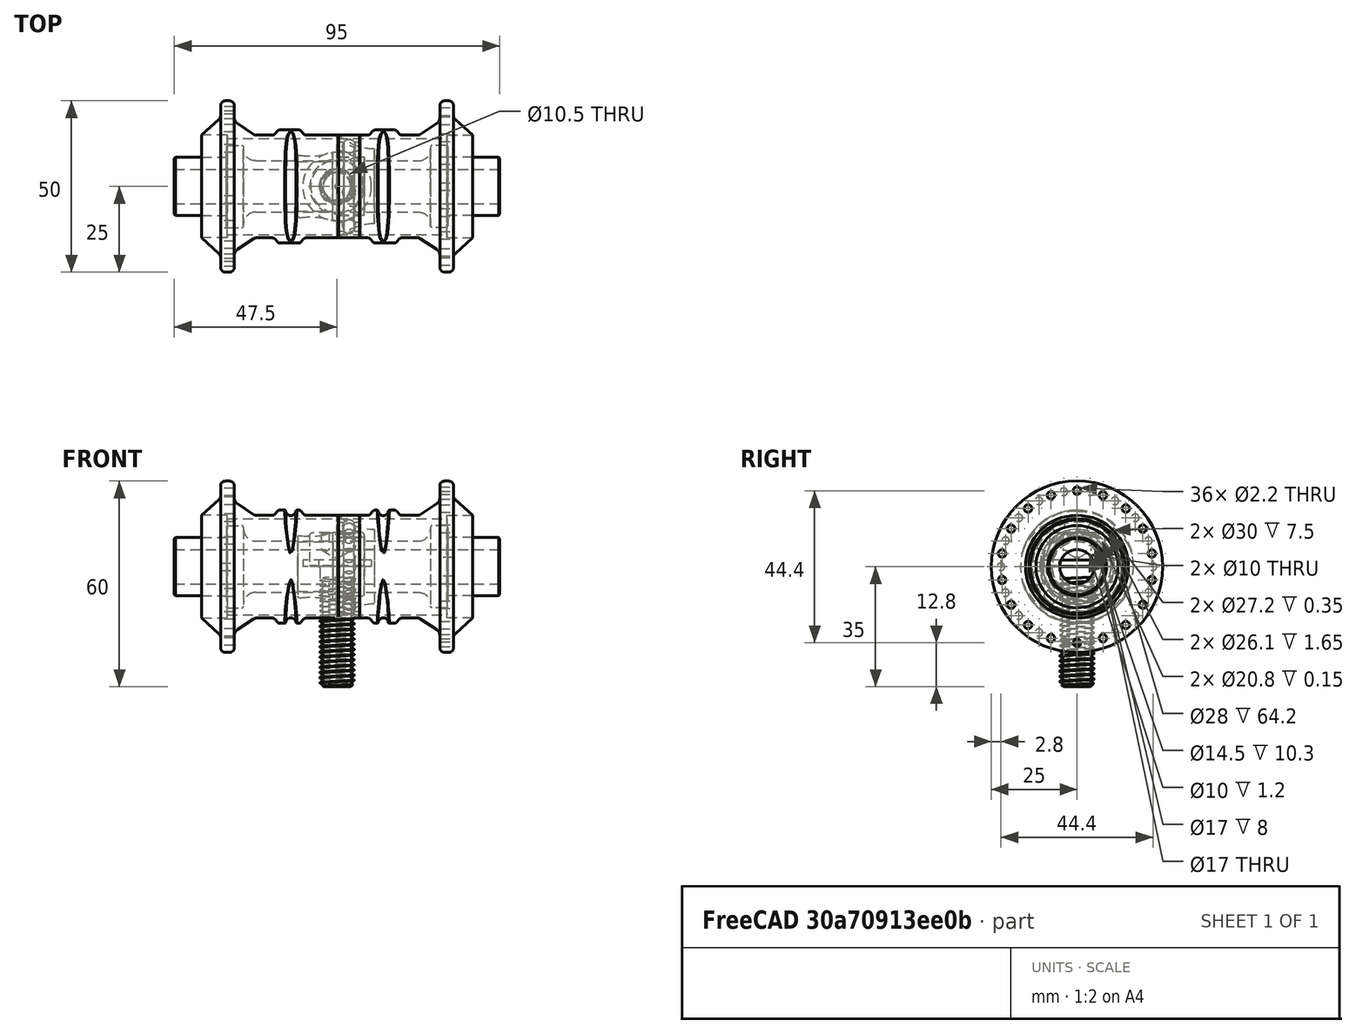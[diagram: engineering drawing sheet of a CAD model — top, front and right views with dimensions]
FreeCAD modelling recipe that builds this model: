
FCSTD DOCUMENT  (FreeCAD 1.0R39109 (Git))
Label: Bike Hub
License: All rights reserved
LicenseURL: https://en.wikipedia.org/wiki/All_rights_reserved
objects: App::FeaturePython×16, Part::Feature×15, Sketcher::SketchObject×13, App::Link×12, PartDesign::Pocket×6, PartDesign::Revolution×4, PartDesign::Body×4, PartDesign::Hole×2, PartDesign::Mirrored×2, PartDesign::PolarPattern×2, PartDesign::Fillet×2, Part::FeaturePython×2, PartDesign::Plane×1, PartDesign::SubtractivePipe×1, App::Part×1, App::DocumentObjectGroup×1, Assembly::JointGroup×1, Assembly::ViewGroup×1, Assembly::AssemblyObject×1
note: 101 computed .brp shape members not serialized (recipe doc carries the construction recipe); baked Part::Feature solids carry a one-line shape summary decoded from their .brp

FEATURE [Sketcher::SketchObject] Sketch
  ArcFitTolerance = 1e-06
  AttachmentSupport = -> [XZ_Plane]
  FullyConstrained = true
  MakeInternals = false
  MapMode = 5
  Placement = pos=(0,0,0) rot=(1,0,0;1.5708rad)
  sketch-geometry (19):
    g0: LineSegment StartX=0 StartY=0 StartZ=0 EndX=-47.5 EndY=0 EndZ=0
    g1: LineSegment StartX=-47.5 StartY=0 StartZ=0 EndX=-47.5 EndY=8.14645 EndZ=0
    g2: LineSegment StartX=-47.1464 StartY=8.5 StartZ=0 EndX=-32.8 EndY=8.5 EndZ=0
    g3: LineSegment StartX=-32.3 StartY=9 StartZ=0 EndX=-32.3 EndY=11.5 EndZ=0
    g4: LineSegment StartX=-31.8 StartY=12 StartZ=0 EndX=-27.8 EndY=12 EndZ=0
    g5: LineSegment StartX=-27.3 StartY=11.5 StartZ=0 EndX=-27.3 EndY=11 EndZ=0
    g6: LineSegment StartX=-23.8 StartY=7.5 StartZ=0 EndX=0 EndY=7.5 EndZ=0
    g7: LineSegment StartX=0 StartY=7.5 StartZ=0 EndX=0 EndY=0 EndZ=0
    g8: ArcOfCircle CenterX=-27.8 CenterY=11.5 CenterZ=0 NormalX=0 NormalY=0 NormalZ=1 AngleXU=0 Radius=0.5 StartAngle=0 EndAngle=1.5708
    g9: GeomPoint [constr] X=-27.3 Y=12 Z=0
    g10: ArcOfCircle CenterX=-23.8 CenterY=11 CenterZ=0 NormalX=0 NormalY=0 NormalZ=1 AngleXU=0 Radius=3.5 StartAngle=3.14159 EndAngle=4.71239
    g11: GeomPoint [constr] X=-27.3 Y=7.5 Z=0
    g12: ArcOfCircle CenterX=-31.8 CenterY=11.5 CenterZ=0 NormalX=0 NormalY=0 NormalZ=1 AngleXU=0 Radius=0.5 StartAngle=1.5708 EndAngle=3.14159
    g13: GeomPoint [constr] X=-32.3 Y=12 Z=0
    g14: ArcOfCircle CenterX=-32.8 CenterY=9 CenterZ=0 NormalX=0 NormalY=0 NormalZ=1 AngleXU=0 Radius=0.5 StartAngle=4.71239 EndAngle=6.28319
    g15: GeomPoint [constr] X=-32.3 Y=8.5 Z=0
    g16: ArcOfCircle [constr] CenterX=-47.1464 CenterY=8.14645 CenterZ=0 NormalX=0 NormalY=0 NormalZ=1 AngleXU=0 Radius=0.353553 StartAngle=1.5708 EndAngle=3.14159
    g17: GeomPoint [constr] X=-47.5 Y=8.5 Z=0
    g18: LineSegment StartX=-47.1464 StartY=8.5 StartZ=0 EndX=-47.5 EndY=8.14645 EndZ=0
  constraints (45):
    c: Coincident(g-1,g0)
    c: PointOnObject(g0,g-1)
    c: Coincident(g0,g1)
    c: Vertical(g1)
    c: Horizontal(g2)
    c: Horizontal(g4)
    c: Vertical(g5)
    c: Horizontal(g6)
    c: Coincident(g6,g7)
    c: Coincident(g7,g0)
    c: Vertical(g7)
    c: Vertical(g3)
    c: DistanceX(g0,g0) = 47.5
    c: DistanceY(g1,g17) = 8.5
    c: Distance(g13,g0) = 12
    c: DistanceX(g13,g-1) = 32.3
    c: DistanceX(g13,g9) = 5
    c: DistanceY(g7,g7) = 7.5
    c: PointOnObject(g9,g4)
    c: PointOnObject(g9,g5)
    c: Tangent(g4,g8) = 1.5708
    c: Tangent(g5,g8) = 1.5708
    c: PointOnObject(g11,g5)
    c: PointOnObject(g11,g6)
    c: Tangent(g5,g10) = -1.5708
    c: Tangent(g6,g10) = -1.5708
    c: PointOnObject(g13,g3)
    c: PointOnObject(g13,g4)
    c: Tangent(g3,g12) = 1.5708
    c: Tangent(g4,g12) = 1.5708
    c: PointOnObject(g15,g2)
    c: PointOnObject(g15,g3)
    c: Tangent(g2,g14) = -1.5708
    c: Tangent(g3,g14) = -1.5708
    c: Radius(g8) = 0.5
    c: Equal(g8,g12)
    c: Equal(g12,g14)
    c: Radius(g10) = 3.5
    c: PointOnObject(g17,g1)
    c: PointOnObject(g17,g2)
    c: Tangent(g1,g16) = 1.5708
    c: Tangent(g2,g16) = 1.5708
    c: Coincident(g18,g1)
    c: Coincident(g18,g2)
    c: Distance(g18,g18) = 0.5
FEATURE [PartDesign::Revolution] Revolution
  Angle = 360
  Angle2 = 60
  Axis = (1,0,0)
  Base = (0,0,0)
  Placement = pos=(0,0,0) rot=(1,0,0;1.5708rad)
  Profile = -> Sketch
  ReferenceAxis = -> X_Axis
  Refine = true
  Suppressed = false
  Type = 0
FEATURE [PartDesign::Hole] Hole
  BaseFeature = -> Revolution
  CustomThreadClearance = 0
  Depth = 117.922
  DepthType = 1
  Diameter = 10
  DrillForDepth = false
  DrillPoint = 1
  DrillPointAngle = 118
  HoleCutCountersinkAngle = 90
  HoleCutCustomValues = false
  HoleCutDepth = 0
  HoleCutDiameter = 6.1
  HoleCutType = 0
  ModelThread = false
  Placement = pos=(0,0,0) rot=(1,0,0;1.5708rad)
  Profile = -> Revolution [Face5]
  Refine = true
  Suppressed = false
  Tapered = false
  TaperedAngle = 90
  ThreadClass = 0
  ThreadDepth = 117.922
  ThreadDepthType = 0
  ThreadDirection = 0
  ThreadFit = 0
  ThreadSize = 0
  ThreadType = 0
  Threaded = false
  UseCustomThreadClearance = false
FEATURE [PartDesign::Mirrored] Mirrored
  BaseFeature = -> Hole
  MirrorPlane = -> YZ_Plane
  Originals = -> [Hole]
  Placement = pos=(0,0,0) rot=(1,0,0;1.5708rad)
  Refine = true
  Suppressed = false
  TransformMode = 1
FEATURE [PartDesign::Body] Body  label="Axle"
  AllowCompound = false
  Group = -> [Sketch,Revolution,Hole,Mirrored]
  Origin = -> Origin
  Tip = -> Mirrored
FEATURE [Sketcher::SketchObject] Sketch001
  ArcFitTolerance = 1e-06
  AttachmentSupport = -> [XZ_Plane001]
  FullyConstrained = true
  MakeInternals = false
  MapMode = 5
  Placement = pos=(0,0,0) rot=(1,0,0;1.5708rad)
  sketch-geometry (31):
    g0: LineSegment StartX=0 StartY=0 StartZ=0 EndX=-39.6 EndY=0 EndZ=0
    g1: LineSegment StartX=-39.6 StartY=0 StartZ=0 EndX=-39.6 EndY=15 EndZ=0
    g2: LineSegment StartX=-39.6 StartY=15 StartZ=0 EndX=-34.4676 EndY=19.5825 EndZ=0
    g3: LineSegment StartX=-34 StartY=20.6268 StartZ=0 EndX=-34 EndY=23.6 EndZ=0
    g4: LineSegment StartX=-32.6 StartY=25 StartZ=0 EndX=-31.4 EndY=25 EndZ=0
    g5: LineSegment StartX=-30 StartY=23.6 StartZ=0 EndX=-30 EndY=20.0704 EndZ=0
    g6: LineSegment StartX=-29.1094 StartY=18.4063 StartZ=0 EndX=-24.2519 EndY=15.1679 EndZ=0
    g7: LineSegment StartX=-23.6972 StartY=15 StartZ=0 EndX=-18.8806 EndY=15 EndZ=0
    g8: LineSegment StartX=-18.0998 StartY=15.3753 StartZ=0 EndX=-17.5002 EndY=16.1247 EndZ=0
    g9: LineSegment StartX=-16.7194 StartY=16.5 StartZ=0 EndX=-11.1806 EndY=16.5 EndZ=0
    g10: LineSegment StartX=-10.3998 StartY=16.1247 StartZ=0 EndX=-9.80024 EndY=15.3753 EndZ=0
    g11: LineSegment StartX=-9.01938 StartY=15 StartZ=0 EndX=0 EndY=15 EndZ=0
    g12: LineSegment StartX=0 StartY=15 StartZ=0 EndX=0 EndY=0 EndZ=0
    g13: ArcOfCircle CenterX=-32.6 CenterY=23.6 CenterZ=0 NormalX=0 NormalY=0 NormalZ=1 AngleXU=0 Radius=1.4 StartAngle=1.5708 EndAngle=3.14159
    g14: GeomPoint [constr] X=-34 Y=25 Z=0
    g15: ArcOfCircle CenterX=-31.4 CenterY=23.6 CenterZ=0 NormalX=0 NormalY=0 NormalZ=1 AngleXU=0 Radius=1.4 StartAngle=0 EndAngle=1.5708
    g16: GeomPoint [constr] X=-30 Y=25 Z=0
    g17: ArcOfCircle CenterX=-35.4 CenterY=20.6268 CenterZ=0 NormalX=0 NormalY=0 NormalZ=1 AngleXU=0 Radius=1.4 StartAngle=5.44124 EndAngle=6.28319
    g18: GeomPoint [constr] X=-34 Y=20 Z=0
    g19: ArcOfCircle CenterX=-28 CenterY=20.0704 CenterZ=0 NormalX=0 NormalY=0 NormalZ=1 AngleXU=0 Radius=2 StartAngle=3.14159 EndAngle=4.12439
    g20: GeomPoint [constr] X=-30 Y=19 Z=0
    g21: ArcOfCircle CenterX=-23.6972 CenterY=16 CenterZ=0 NormalX=0 NormalY=0 NormalZ=1 AngleXU=0 Radius=1 StartAngle=4.12439 EndAngle=4.71239
    g22: GeomPoint [constr] X=-24 Y=15 Z=0
    g23: ArcOfCircle CenterX=-18.8806 CenterY=16 CenterZ=0 NormalX=0 NormalY=0 NormalZ=1 AngleXU=0 Radius=1 StartAngle=4.71239 EndAngle=5.60844
    g24: GeomPoint [constr] X=-18.4 Y=15 Z=0
    g25: ArcOfCircle CenterX=-16.7194 CenterY=15.5 CenterZ=0 NormalX=0 NormalY=0 NormalZ=1 AngleXU=0 Radius=1 StartAngle=1.5708 EndAngle=2.46685
    g26: GeomPoint [constr] X=-17.2 Y=16.5 Z=0
    g27: ArcOfCircle CenterX=-11.1806 CenterY=15.5 CenterZ=0 NormalX=0 NormalY=0 NormalZ=1 AngleXU=0 Radius=1 StartAngle=0.674741 EndAngle=1.5708
    g28: GeomPoint [constr] X=-10.7 Y=16.5 Z=0
    g29: ArcOfCircle CenterX=-9.01938 CenterY=16 CenterZ=0 NormalX=0 NormalY=0 NormalZ=1 AngleXU=0 Radius=1 StartAngle=3.81633 EndAngle=4.71239
    g30: GeomPoint [constr] X=-9.5 Y=15 Z=0
  constraints (74):
    c: Coincident(g-1,g0)
    c: PointOnObject(g0,g-1)
    c: Coincident(g0,g1)
    c: Vertical(g1)
    c: Coincident(g1,g2)
    c: Vertical(g3)
    c: Horizontal(g4)
    c: Vertical(g5)
    c: Horizontal(g7)
    c: Horizontal(g9)
    c: Horizontal(g11)
    c: Coincident(g11,g12)
    c: Coincident(g12,g0)
    c: Vertical(g12)
    c: DistanceX(g0,g0) = 39.6
    c: Distance(g0,g4) = 25
    c: DistanceY(g-1,g1) = 15
    c: DistanceY(g-1,g18) = 20
    c: DistanceY(g-1,g20) = 19
    c: DistanceX(g14,g16) = 4
    c: DistanceX(g14,g-1) = 34
    c: DistanceX(g22,g-1) = 24
    c: DistanceX(g26,g28) = 6.5
    c: DistanceX(g30,g11) = 9.5
    c: DistanceX(g28,g-1) = 10.7
    c: DistanceY(g-1,g28) = 16.5
    c: PointOnObject(g14,g3)
    c: PointOnObject(g14,g4)
    c: Tangent(g3,g13) = 1.5708
    c: Tangent(g4,g13) = 1.5708
    c: PointOnObject(g16,g4)
    c: PointOnObject(g16,g5)
    c: Tangent(g4,g15) = 1.5708
    c: Tangent(g5,g15) = 1.5708
    c: PointOnObject(g18,g2)
    c: PointOnObject(g18,g3)
    c: Tangent(g2,g17) = -1.5708
    c: Tangent(g3,g17) = -1.5708
    c: PointOnObject(g20,g5)
    c: PointOnObject(g20,g6)
    c: Tangent(g5,g19) = -1.5708
    c: Tangent(g6,g19) = -1.5708
    c: Equal(g17,g13)
    c: Equal(g13,g15)
    c: Radius(g13) = 1.4
    c: Radius(g19) = 2
    c: PointOnObject(g22,g6)
    c: PointOnObject(g22,g7)
    c: Tangent(g6,g21) = -1.5708
    c: Tangent(g7,g21) = -1.5708
    c: PointOnObject(g24,g7)
    c: PointOnObject(g24,g8)
    c: Tangent(g7,g23) = -1.5708
    c: Tangent(g8,g23) = -1.5708
    c: PointOnObject(g26,g8)
    c: PointOnObject(g26,g9)
    c: Tangent(g8,g25) = 1.5708
    c: Tangent(g9,g25) = 1.5708
    c: PointOnObject(g28,g9)
    c: PointOnObject(g28,g10)
    c: Tangent(g9,g27) = 1.5708
    c: Tangent(g10,g27) = 1.5708
    c: PointOnObject(g30,g10)
    c: PointOnObject(g30,g11)
    c: Tangent(g10,g29) = -1.5708
    c: Tangent(g11,g29) = -1.5708
    c: Radius(g21) = 1
    c: Horizontal(g11,g22)
    c: Equal(g21,g23)
    c: Equal(g23,g25)
    c: Equal(g25,g27)
    c: Equal(g27,g29)
    c: Horizontal(g11,g1)
    c: Equal(g8,g10)
FEATURE [PartDesign::Revolution] Revolution001
  Angle = 360
  Angle2 = 60
  Axis = (1,0,0)
  Base = (0,0,0)
  Placement = pos=(0,0,0) rot=(1,0,0;1.5708rad)
  Profile = -> Sketch001
  ReferenceAxis = -> X_Axis001
  Refine = true
  Suppressed = false
  Type = 0
FEATURE [Sketcher::SketchObject] Sketch002
  ArcFitTolerance = 1e-06
  AttachmentSupport = -> [Revolution001]
  FullyConstrained = true
  MakeInternals = false
  MapMode = 5
  Placement = pos=(-39.6,0,0) rot=(0.707107,0,-0.707107;3.14159rad)
  sketch-geometry (1):
    g0: Circle CenterX=0 CenterY=0 CenterZ=0 NormalX=0 NormalY=0 NormalZ=1 AngleXU=0 Radius=15
  constraints (2):
    c: Diameter(g0) = 30
    c: Coincident(g0,g-1)
FEATURE [PartDesign::Pocket] Pocket
  BaseFeature = -> Revolution001
  Direction = (1,0,2e-16)
  Length = 7.5
  Length2 = 5
  Placement = pos=(0,0,0) rot=(1,0,0;1.5708rad)
  Profile = -> Sketch002
  ReferenceAxis = -> Sketch002 [N_Axis]
  Refine = true
  Suppressed = false
  Type = 0
FEATURE [Sketcher::SketchObject] Sketch003
  ArcFitTolerance = 1e-06
  AttachmentSupport = -> [Pocket]
  FullyConstrained = true
  MakeInternals = false
  MapMode = 5
  Placement = pos=(0,0,0) rot=(0.707107,0,0.707107;3.14159rad)
  sketch-geometry (1):
    g0: Circle CenterX=0 CenterY=0 CenterZ=0 NormalX=0 NormalY=0 NormalZ=1 AngleXU=0 Radius=14
  constraints (2):
    c: Diameter(g0) = 28
    c: Coincident(g0,g-1)
FEATURE [PartDesign::Pocket] Pocket001
  BaseFeature = -> Pocket
  Direction = (-1,0,2e-16)
  Length = 5
  Length2 = 5
  Placement = pos=(0,0,0) rot=(1,0,0;1.5708rad)
  Profile = -> Sketch003
  ReferenceAxis = -> Sketch003 [N_Axis]
  Refine = true
  Suppressed = false
  Type = 1
FEATURE [PartDesign::Plane] DatumPlane
  AttachmentOffset = pos=(0,0,-13.5) rot=(0,0,1;0rad)
  AttachmentSupport = -> [Pocket001]
  Length = 60
  MapMode = 5
  Placement = pos=(-13.5,0,3e-15) rot=(0.707107,0,0.707107;3.14159rad)
  ResizeMode = 0
  Width = 60
FEATURE [Sketcher::SketchObject] Sketch004
  ArcFitTolerance = 1e-06
  AttachmentSupport = -> [DatumPlane]
  FullyConstrained = true
  MakeInternals = false
  MapMode = 5
  Placement = pos=(-13.5,0,3e-15) rot=(0.707107,0,0.707107;3.14159rad)
  sketch-geometry (5):
    g0: Ellipse CenterX=0 CenterY=0 CenterZ=0 NormalX=0 NormalY=0 NormalZ=1 MajorRadius=18.1 MinorRadius=16.4 AngleXU=-1.5708
    g1: LineSegment [constr] StartX=6.27002e-06 StartY=-18.1 StartZ=0 EndX=-6.27002e-06 EndY=18.1 EndZ=0
    g2: LineSegment [constr] StartX=16.4 StartY=5.68113e-06 StartZ=0 EndX=-16.4 EndY=-5.68113e-06 EndZ=0
    g3: GeomPoint [constr] X=2.65292e-06 Y=-7.65833 Z=0
    g4: GeomPoint [constr] X=-2.65292e-06 Y=7.65833 Z=0
  constraints (5):
    c: InternalAlignment(g1-g4 -> g0) x4
    c: Distance(g0,g2) = 16.4
    c: Angle(g2) = 3.14159
    c: Distance(g0,g1) = 18.1
    c: Coincident(g0,g-1)
FEATURE [Sketcher::SketchObject] Sketch005
  ArcFitTolerance = 1e-06
  AttachmentSupport = -> [XY_Plane001]
  ExternalGeometry = -> [Sketch004]
  FullyConstrained = true
  MakeInternals = false
  MapMode = 5
  sketch-geometry (1):
    g0: Circle CenterX=-13.5 CenterY=18.1 CenterZ=0 NormalX=0 NormalY=0 NormalZ=1 AngleXU=0 Radius=1.5
  constraints (2):
    c: Diameter(g0) = 3
    c: Coincident(g0,g-3)
FEATURE [PartDesign::SubtractivePipe] SubtractivePipe
  AuxilleryCurvelinear = true
  AuxillerySpineTangent = false
  BaseFeature = -> Pocket001
  Binormal = (0,0,0)
  Mode = 0
  Placement = pos=(0,0,0) rot=(1,0,0;1.5708rad)
  Profile = -> Sketch005
  Refine = true
  Spine = -> Sketch004
  SpineTangent = false
  Suppressed = false
  Transformation = 0
  Transition = 0
FEATURE [PartDesign::Mirrored] Mirrored001
  BaseFeature = -> SubtractivePipe
  MirrorPlane = -> Sketch005 [V_Axis]
  Originals = -> [SubtractivePipe]
  Placement = pos=(0,0,0) rot=(1,0,0;1.5708rad)
  Refine = true
  Suppressed = false
  TransformMode = 1
FEATURE [Sketcher::SketchObject] Sketch006
  ArcFitTolerance = 1e-06
  AttachmentSupport = -> [Mirrored001]
  FullyConstrained = true
  MakeInternals = false
  MapMode = 5
  Placement = pos=(-34,0,0) rot=(0.707107,0,-0.707107;3.14159rad)
  sketch-geometry (1):
    g0: Circle CenterX=0 CenterY=22.2 CenterZ=0 NormalX=0 NormalY=0 NormalZ=1 AngleXU=0 Radius=1.1
  constraints (3):
    c: Diameter(g0) = 2.2
    c: PointOnObject(g0,g-2)
    c: DistanceY(g-1,g0) = 22.2
FEATURE [PartDesign::Pocket] Pocket002
  BaseFeature = -> Mirrored001
  Direction = (1,0,2e-16)
  Length = 0
  Length2 = 5
  Placement = pos=(0,0,0) rot=(1,0,0;1.5708rad)
  Profile = -> Sketch006
  ReferenceAxis = -> Sketch006 [N_Axis]
  Refine = true
  Suppressed = false
  Type = 3
  UpToFace = -> Mirrored001 [Face14]
FEATURE [PartDesign::PolarPattern] PolarPattern
  Angle = 360
  Axis = -> Sketch006 [N_Axis]
  BaseFeature = -> Pocket002
  Mode = 0
  Occurrences = 18
  Offset = 120
  Originals = -> [Pocket002]
  Placement = pos=(0,0,0) rot=(1,0,0;1.5708rad)
  Refine = true
  Suppressed = false
  TransformMode = 0
FEATURE [Sketcher::SketchObject] Sketch007
  ArcFitTolerance = 1e-06
  AttachmentSupport = -> [PolarPattern]
  FullyConstrained = true
  MakeInternals = false
  MapMode = 5
  Placement = pos=(34,0,0) rot=(0.707107,0,0.707107;3.14159rad)
  sketch-geometry (2):
    g0: Circle CenterX=-3.85499 CenterY=21.8627 CenterZ=0 NormalX=0 NormalY=0 NormalZ=1 AngleXU=0 Radius=1.1
    g1: LineSegment [constr] StartX=-3.85499 StartY=21.8627 StartZ=0 EndX=4e-16 EndY=0 EndZ=0
  constraints (5):
    c: Diameter(g0) = 2.2
    c: Coincident(g1,g0)
    c: Coincident(g1,g-1)
    c: Distance(g1,g1) = 22.2
    c: Angle(g-2,g1) = 0.174533
FEATURE [PartDesign::Pocket] Pocket003
  BaseFeature = -> PolarPattern
  Direction = (-1,0,2e-16)
  Length = 0
  Length2 = 5
  Placement = pos=(0,0,0) rot=(1,0,0;1.5708rad)
  Profile = -> Sketch007
  ReferenceAxis = -> Sketch007 [N_Axis]
  Refine = true
  Suppressed = false
  Type = 3
  UpToFace = -> PolarPattern [Face53]
FEATURE [PartDesign::PolarPattern] PolarPattern001
  Angle = 360
  Axis = -> Sketch007 [N_Axis]
  BaseFeature = -> Pocket003
  Mode = 0
  Occurrences = 18
  Offset = 120
  Originals = -> [Pocket003]
  Placement = pos=(0,0,0) rot=(1,0,0;1.5708rad)
  Refine = true
  Suppressed = false
  TransformMode = 0
FEATURE [PartDesign::Fillet] Fillet
  Base = -> PolarPattern001 [Edge9,Edge15,Edge41,Edge35]
  BaseFeature = -> PolarPattern001
  Placement = pos=(0,0,0) rot=(1,0,0;1.5708rad)
  Radius = 0.3
  Refine = true
  SupportTransform = false
  Suppressed = false
  UseAllEdges = false
FEATURE [PartDesign::Body] Body001  label="Hub Cage"
  AllowCompound = false
  Group = -> [Sketch001,Revolution001,Sketch002,Pocket,Sketch003,Pocket001,DatumPlane,Sketch004,Sketch005,SubtractivePipe,Mirrored001,Sketch006,Pocket002,PolarPattern,Sketch007,Pocket003,PolarPattern001,Fillet]
  Origin = -> Origin001
  Tip = -> Fillet
FEATURE [Sketcher::SketchObject] Sketch008
  ArcFitTolerance = 1e-06
  AttachmentSupport = -> [XZ_Plane002]
  FullyConstrained = true
  MakeInternals = false
  MapMode = 5
  Placement = pos=(0,0,0) rot=(1,0,0;1.5708rad)
  sketch-geometry (8):
    g0: LineSegment StartX=0 StartY=0 StartZ=0 EndX=10.9 EndY=0 EndZ=0
    g1: LineSegment StartX=0 StartY=0 StartZ=0 EndX=0 EndY=10.9 EndZ=0
    g2: LineSegment StartX=0 StartY=10.9 StartZ=0 EndX=0.3 EndY=10.9 EndZ=0
    g3: LineSegment StartX=0.3 StartY=10.9 StartZ=0 EndX=0.3 EndY=15 EndZ=0
    g4: LineSegment StartX=0.3 StartY=15 StartZ=0 EndX=0.5 EndY=15 EndZ=0
    g5: LineSegment StartX=10.9 StartY=0 StartZ=0 EndX=10.9 EndY=10.9 EndZ=0
    g6: ArcOfCircle CenterX=10.9 CenterY=26.1402 CenterZ=0 NormalX=0 NormalY=0 NormalZ=1 AngleXU=0 Radius=15.2402 StartAngle=3.96134 EndAngle=4.71239
    g7: LineSegment [constr] StartX=10.9 StartY=10.9 StartZ=0 EndX=20.01 EndY=10.9 EndZ=0
  constraints (24):
    c: Coincident(g-1,g0)
    c: PointOnObject(g0,g-1)
    c: Coincident(g0,g1)
    c: PointOnObject(g1,g-2)
    c: Coincident(g1,g2)
    c: Horizontal(g2)
    c: Coincident(g2,g3)
    c: DistanceX(g0,g0) = 10.9
    c: DistanceY(g1,g1) = 10.9
    c: Coincident(g4,g3)
    c: Vertical(g3)
    c: Horizontal(g4)
    c: DistanceX(g2,g2) = 0.3
    c: DistanceX(g4,g4) = 0.2
    c: DistanceY(g-1,g3) = 15
    c: Coincident(g0,g5)
    c: Vertical(g5)
    c: Coincident(g6,g5)
    c: Coincident(g6,g4)
    c: Coincident(g7,g5)
    c: Horizontal(g7)
    c: Tangent(g6,g7)
    c: Horizontal(g5,g2)
    c: DistanceX(g7,g7) = 9.11
FEATURE [PartDesign::Revolution] Revolution002
  Angle = 360
  Angle2 = 60
  Axis = (1,0,0)
  Base = (0,0,0)
  Placement = pos=(0,0,0) rot=(1,0,0;1.5708rad)
  Profile = -> Sketch008
  ReferenceAxis = -> X_Axis002
  Refine = true
  Suppressed = false
  Type = 0
FEATURE [Sketcher::SketchObject] Sketch009
  ArcFitTolerance = 1e-06
  AttachmentSupport = -> [Revolution002]
  FullyConstrained = true
  MakeInternals = false
  MapMode = 5
  Placement = pos=(0,0,0) rot=(0.707107,0,-0.707107;3.14159rad)
  sketch-geometry (1):
    g0: Circle CenterX=0 CenterY=0 CenterZ=0 NormalX=0 NormalY=0 NormalZ=1 AngleXU=0 Radius=8.5
  constraints (2):
    c: Coincident(g0,g-1)
    c: Diameter(g0) = 17
FEATURE [PartDesign::Pocket] Pocket004
  BaseFeature = -> Revolution002
  Direction = (1,0,2e-16)
  Length = 8
  Length2 = 5
  Placement = pos=(0,0,0) rot=(1,0,0;1.5708rad)
  Profile = -> Sketch009
  ReferenceAxis = -> Sketch009 [N_Axis]
  Refine = true
  Suppressed = false
  Type = 0
FEATURE [Sketcher::SketchObject] Sketch010
  ArcFitTolerance = 1e-06
  AttachmentSupport = -> [Pocket004]
  FullyConstrained = true
  MakeInternals = false
  MapMode = 5
  Placement = pos=(10.9,0,0) rot=(0.707107,0,0.707107;3.14159rad)
  sketch-geometry (1):
    g0: Circle CenterX=0 CenterY=0 CenterZ=0 NormalX=0 NormalY=0 NormalZ=1 AngleXU=0 Radius=5
  constraints (2):
    c: Coincident(g0,g-1)
    c: Diameter(g0) = 10
FEATURE [Part::Feature] Part__Feature  label="69032RS Inner ring"
  shape: bbox 7.014 x 25.44 x 25.44 mm, 8 faces (baked)
FEATURE [Part::Feature] Part__Feature001  label="69032RS Outer ring"
  shape: bbox 7.014 x 32.49 x 32.49 mm, 12 faces (baked)
FEATURE [Part::Feature] Part__Feature002  label="69032RS Ball"
  Placement = pos=(3.5,11.75,0) rot=(0.707107,0,-0.707107;3.14159rad)
  shape: bbox 3.97 x 3.97 x 3.97 mm, 1 faces (baked)
FEATURE [Part::Feature] Part__Feature003  label="69032RS Ball001"
  Placement = pos=(3.5,9.88473,6.35253) rot=(0.707107,0,-0.707107;3.14159rad)
  shape: bbox 3.97 x 3.97 x 3.97 mm, 1 faces (baked)
FEATURE [Part::Feature] Part__Feature004  label="69032RS Ball002"
  Placement = pos=(3.5,4.88113,10.6882) rot=(0.707107,0,-0.707107;3.14159rad)
  shape: bbox 3.97 x 3.97 x 3.97 mm, 1 faces (baked)
FEATURE [Part::Feature] Part__Feature005  label="69032RS Ball003"
  Placement = pos=(3.5,-1.6722,11.6304) rot=(0.707107,0,-0.707107;3.14159rad)
  shape: bbox 3.97 x 3.97 x 3.97 mm, 1 faces (baked)
FEATURE [Part::Feature] Part__Feature006  label="69032RS Ball004"
  Placement = pos=(3.5,-7.69461,8.88006) rot=(0.707107,0,-0.707107;3.14159rad)
  shape: bbox 3.97 x 3.97 x 3.97 mm, 1 faces (baked)
FEATURE [Part::Feature] Part__Feature007  label="69032RS Ball005"
  Placement = pos=(3.5,-11.274,3.31036) rot=(0.707107,0,-0.707107;3.14159rad)
  shape: bbox 3.97 x 3.97 x 3.97 mm, 1 faces (baked)
FEATURE [Part::Feature] Part__Feature008  label="69032RS Ball006"
  Placement = pos=(3.5,-11.274,-3.31036) rot=(0.707107,0,-0.707107;3.14159rad)
  shape: bbox 3.97 x 3.97 x 3.97 mm, 1 faces (baked)
FEATURE [Part::Feature] Part__Feature009  label="69032RS Ball007"
  Placement = pos=(3.5,-7.69461,-8.88006) rot=(0.707107,0,-0.707107;3.14159rad)
  shape: bbox 3.97 x 3.97 x 3.97 mm, 1 faces (baked)
FEATURE [Part::Feature] Part__Feature010  label="69032RS Ball008"
  Placement = pos=(3.5,-1.6722,-11.6304) rot=(0.707107,0,-0.707107;3.14159rad)
  shape: bbox 3.97 x 3.97 x 3.97 mm, 1 faces (baked)
FEATURE [Part::Feature] Part__Feature011  label="69032RS Ball009"
  Placement = pos=(3.5,4.88113,-10.6882) rot=(0.707107,0,-0.707107;3.14159rad)
  shape: bbox 3.97 x 3.97 x 3.97 mm, 1 faces (baked)
FEATURE [Part::Feature] Part__Feature012  label="69032RS Ball010"
  Placement = pos=(3.5,9.88473,-6.35253) rot=(0.707107,0,-0.707107;3.14159rad)
  shape: bbox 3.97 x 3.97 x 3.97 mm, 1 faces (baked)
FEATURE [Part::Feature] Part__Feature013  label="69032RS Seal"
  Placement = pos=(0.2,0,0) rot=(0,0,1;0rad)
  shape: bbox 0.15 x 27.2 x 27.2 mm, 4 faces (baked)
FEATURE [Part::Feature] Part__Feature014  label="69032RS Seal001"
  Placement = pos=(6.65,0,0) rot=(0,0,1;0rad)
  shape: bbox 0.15 x 27.2 x 27.2 mm, 4 faces (baked)
FEATURE [App::Part] _9032RS  label="Bearing"
  Group = -> [Part__Feature,Part__Feature001,Part__Feature002,Part__Feature003,Part__Feature004,Part__Feature005,Part__Feature006,Part__Feature007,Part__Feature008,Part__Feature009,Part__Feature010,Part__Feature011,Part__Feature012,Part__Feature013,Part__Feature014]
  Origin = -> Origin003
FEATURE [Part::FeaturePython] Washer  label="M10-Washer"  # WARN: FeaturePython — macro-defined, semantics opaque (R4)
  Diameter = 9
  Invert = false
  MatchOuter = false
  OffsetAngle = 0
  Type = 8
FEATURE [Part::FeaturePython] Screw  label="M10x35-Screw"  # WARN: FeaturePython — macro-defined, semantics opaque (R4)
  Diameter = 9
  Invert = false
  LeftHanded = false
  Length = 4
  LengthCustom = 35
  MatchOuter = false
  OffsetAngle = 0
  Thread = true
  Type = 75
FEATURE [Sketcher::SketchObject] Sketch011
  ArcFitTolerance = 1e-06
  AttachmentSupport = -> [XZ_Plane004]
  FullyConstrained = true
  MakeInternals = false
  MapMode = 5
  Placement = pos=(0,0,0) rot=(1,0,0;1.5708rad)
  sketch-geometry (5):
    g0: LineSegment StartX=0 StartY=0 StartZ=0 EndX=-11.5 EndY=0 EndZ=0
    g1: LineSegment StartX=-11.5 StartY=0 StartZ=0 EndX=-11.5 EndY=9.2 EndZ=0
    g2: LineSegment StartX=0 StartY=0 StartZ=0 EndX=0 EndY=10 EndZ=0
    g3: LineSegment StartX=0 StartY=10 StartZ=0 EndX=-1.3 EndY=10 EndZ=0
    g4: ArcOfCircle CenterX=-7.9118 CenterY=28.8755 CenterZ=0 NormalX=0 NormalY=0 NormalZ=1 AngleXU=0 Radius=20 StartAngle=4.532 EndAngle=5.04932
  constraints (15):
    c: Coincident(g-1,g0)
    c: PointOnObject(g0,g-1)
    c: Coincident(g0,g1)
    c: Vertical(g1)
    c: Coincident(g0,g2)
    c: PointOnObject(g2,g-2)
    c: Coincident(g2,g3)
    c: Horizontal(g3)
    c: Coincident(g4,g3)
    c: Coincident(g4,g1)
    c: DistanceX(g0,g0) = 11.5
    c: DistanceY(g1,g1) = 9.2
    c: DistanceY(g2,g2) = 10
    c: DistanceX(g3,g3) = 1.3
    c: Radius(g4) = 20
FEATURE [PartDesign::Revolution] Revolution003
  Angle = 360
  Angle2 = 60
  Axis = (1,0,0)
  Base = (0,0,0)
  Placement = pos=(0,0,0) rot=(1,0,0;1.5708rad)
  Profile = -> Sketch011
  ReferenceAxis = -> X_Axis004
  Refine = true
  Suppressed = false
  Type = 0
FEATURE [Sketcher::SketchObject] Sketch012
  ArcFitTolerance = 1e-06
  AttachmentSupport = -> [Revolution003]
  FullyConstrained = true
  MakeInternals = false
  MapMode = 5
  Placement = pos=(-11.5,0,0) rot=(0.707107,0,-0.707107;3.14159rad)
  sketch-geometry (1):
    g0: Circle CenterX=0 CenterY=0 CenterZ=0 NormalX=0 NormalY=0 NormalZ=1 AngleXU=0 Radius=5
  constraints (2):
    c: Diameter(g0) = 10
    c: Coincident(g0,g-1)
FEATURE [PartDesign::Hole] Hole001
  BaseFeature = -> Revolution003
  CustomThreadClearance = 0
  Depth = 61.6685
  DepthType = 1
  Diameter = 10
  DrillForDepth = false
  DrillPoint = 1
  DrillPointAngle = 118
  HoleCutCountersinkAngle = 90
  HoleCutCustomValues = false
  HoleCutDepth = 10.3
  HoleCutDiameter = 14.5
  HoleCutType = 1
  ModelThread = false
  Placement = pos=(0,0,0) rot=(1,0,0;1.5708rad)
  Profile = -> Sketch012
  Refine = true
  Suppressed = false
  Tapered = false
  TaperedAngle = 90
  ThreadClass = 0
  ThreadDepth = 61.6685
  ThreadDepthType = 0
  ThreadDirection = 0
  ThreadFit = 0
  ThreadSize = 0
  ThreadType = 0
  Threaded = false
  UseCustomThreadClearance = false
FEATURE [PartDesign::Fillet] Fillet001
  Base = -> Hole001 [Edge1]
  BaseFeature = -> Hole001
  Placement = pos=(0,0,0) rot=(1,0,0;1.5708rad)
  Radius = 0.5
  Refine = true
  SupportTransform = false
  Suppressed = false
  UseAllEdges = false
FEATURE [PartDesign::Body] Body003  label="Bolt Cover"
  AllowCompound = false
  Group = -> [Sketch011,Revolution003,Sketch012,Hole001,Fillet001]
  Origin = -> Origin004
  Tip = -> Fillet001
FEATURE [App::Link] Axle  label="Axle001"
  LinkPlacement = pos=(0,0.00370701,0.00298656) rot=(0,0,1;0rad)
  LinkedObject = -> Body
  Placement = pos=(0,0.00370701,0.00298656) rot=(0,0,1;0rad)
FEATURE [App::FeaturePython] GroundedJoint  # Assembly grounded joint (typed FeaturePython)
  ObjectToGround = -> Axle
FEATURE [App::Link] Hub_Cage  label="Hub Cage001"
  LinkPlacement = pos=(0,7.64805e-07,7.64805e-07) rot=(1,0,0;1.86574rad)
  LinkedObject = -> Body001
  Placement = pos=(0,7.64805e-07,7.64805e-07) rot=(1,0,0;1.86574rad)
FEATURE [App::Link] Bearing  label="Bearing001"
  LinkPlacement = pos=(60.6496,0.00148296,0.00045047) rot=(-1,0,0;1.27585rad)
  LinkedObject = -> _9032RS
  Placement = pos=(60.6496,0.00148296,0.00045047) rot=(-1,0,0;1.27585rad)
FEATURE [App::Link] Bearing001  label="Bearing002"
  LinkPlacement = pos=(-67.6496,0.00148296,0.00045047) rot=(-1,0,0;1.27585rad)
  LinkedObject = -> _9032RS
  Placement = pos=(-67.6496,0.00148296,0.00045047) rot=(-1,0,0;1.27585rad)
FEATURE [PartDesign::Pocket] Pocket005
  BaseFeature = -> Pocket004
  Direction = (-1,0,2e-16)
  Length = 5
  Length2 = 5
  Placement = pos=(0,0,0) rot=(1,0,0;1.5708rad)
  Profile = -> Sketch010
  ReferenceAxis = -> Sketch010 [N_Axis]
  Refine = true
  Suppressed = false
  Type = 1
FEATURE [PartDesign::Body] Body002  label="Bearing Cover"
  AllowCompound = false
  Group = -> [Sketch008,Revolution002,Sketch009,Pocket004,Sketch010,Pocket005]
  Origin = -> Origin002
  Tip = -> Pocket005
FEATURE [App::DocumentObjectGroup] Group  label="Parts"
  Group = -> [Body,Body001,Body002,_9032RS,Washer,Screw,Body003]
FEATURE [App::Link] Bearing_Cover  label="Bearing Cover001"
  LinkPlacement = pos=(74.8272,0.00148296,0.000451235) rot=(1,0,0;1.86574rad)
  LinkedObject = -> Body002
  Placement = pos=(74.8272,0.00148296,0.000451235) rot=(1,0,0;1.86574rad)
FEATURE [App::Link] Bearing_Cover001  label="Bearing Cover002"
  LinkPlacement = pos=(-74.8272,0.00148296,0.000451235) rot=(0,0.803332,-0.595532;3.14159rad)
  LinkedObject = -> Body002
  Placement = pos=(-74.8272,0.00148296,0.000451235) rot=(0,0.803332,-0.595532;3.14159rad)
FEATURE [App::Link] M10_Washer  label="M10-Washer001"
  LinkPlacement = pos=(90.8998,0.00222405,0.00067647) rot=(-0.51167,0.690208,-0.51167;1.93335rad)
  LinkedObject = -> Washer
  Placement = pos=(90.8998,0.00222405,0.00067647) rot=(-0.51167,0.690208,-0.51167;1.93335rad)
FEATURE [App::Link] M10_Washer001  label="M10-Washer002"
  LinkPlacement = pos=(-92.8998,0.00222405,0.00067647) rot=(-0.51167,0.690208,-0.51167;1.93335rad)
  LinkedObject = -> Washer
  Placement = pos=(-92.8998,0.00222405,0.00067647) rot=(-0.51167,0.690208,-0.51167;1.93335rad)
FEATURE [App::Link] M10x35_Screw  label="M10x35-Screw001"
  LinkPlacement = pos=(150.84,0.00251118,0.000765952) rot=(-0.513899,0.693215,-0.513899;1.93335rad)
  LinkedObject = -> Screw
  Placement = pos=(150.84,0.00251118,0.000765952) rot=(-0.513899,0.693215,-0.513899;1.93335rad)
FEATURE [App::Link] M10x35_Screw001  label="M10x35-Screw002"
  LinkPlacement = pos=(-148.84,0.00252118,0.000755952) rot=(0.629006,-0.466299,-0.629006;2.27227rad)
  LinkedObject = -> Screw
  Placement = pos=(-148.84,0.00252118,0.000755952) rot=(0.629006,-0.466299,-0.629006;2.27227rad)
FEATURE [App::Link] Bolt_Cover  label="Bolt Cover001"
  LinkPlacement = pos=(98.313,0.00415748,-0.000356017) rot=(0,0.989146,0.146937;3.14159rad)
  LinkedObject = -> Body003
  Placement = pos=(98.313,0.00415748,-0.000356017) rot=(0,0.989146,0.146937;3.14159rad)
FEATURE [App::Link] Bolt_Cover001  label="Bolt Cover002"
  LinkPlacement = pos=(-98.313,0.00325654,0.00260913) rot=(1,0,0;0.294941rad)
  LinkedObject = -> Body003
  Placement = pos=(-98.313,0.00325654,0.00260913) rot=(1,0,0;0.294941rad)
FEATURE [App::FeaturePython] Joint  label="Revolute"  # Assembly joint (typed FeaturePython)
  Activated = true
  AngleMax = 0
  AngleMin = 0
  Detach1 = false
  Detach2 = false
  Distance = 0
  Distance2 = 0
  EnableAngleMax = false
  EnableAngleMin = false
  EnableLengthMax = false
  EnableLengthMin = false
  JointType = 1 (Revolute)
  LengthMax = 0
  LengthMin = 0
  Placement1 = pos=(0,0,0) rot=(-0.707107,0,-0.707107;3.14159rad)
  Placement2 = pos=(0,0,0) rot=(0.707107,0,0.707107;3.14159rad)
  Reference1 = -> Assembly [Hub_Cage.Fillet.Face14,Hub_Cage.Fillet.Face14]
  Reference2 = -> Assembly [Axle.Mirrored.Face11,Axle.Mirrored.Face11]
FEATURE [App::FeaturePython] Joint001  label="Fixed"  # Assembly joint (typed FeaturePython)
  Activated = true
  AngleMax = 0
  AngleMin = 0
  Detach1 = false
  Detach2 = false
  Distance = 0
  Distance2 = 0
  EnableAngleMax = false
  EnableAngleMin = false
  EnableLengthMax = false
  EnableLengthMin = false
  JointType = 0 (Fixed)
  LengthMax = 0
  LengthMin = 0
  Placement1 = pos=(7,0,0) rot=(0,1,0;1.5708rad)
  Placement2 = pos=(-32.1,0,7.1e-15) rot=(-0.707107,0,-0.707107;3.14159rad)
  Reference1 = -> Assembly [Bearing001.Part__Feature001.Edge15,Bearing001.Part__Feature001.Edge15]
  Reference2 = -> Assembly [Hub_Cage.Fillet.Edge133,Hub_Cage.Fillet.Edge133]
FEATURE [App::FeaturePython] Joint002  label="Fixed001"  # Assembly joint (typed FeaturePython)
  Activated = true
  AngleMax = 0
  AngleMin = 0
  Detach1 = false
  Detach2 = false
  Distance = 0
  Distance2 = 0
  EnableAngleMax = false
  EnableAngleMin = false
  EnableLengthMax = false
  EnableLengthMin = false
  JointType = 0 (Fixed)
  LengthMax = 0
  LengthMin = 0
  Placement1 = pos=(0,0,0) rot=(0,1,0;1.5708rad)
  Placement2 = pos=(32.1,0,7.1e-15) rot=(-0.707107,0,-0.707107;3.14159rad)
  Reference1 = -> Assembly [Bearing.Part__Feature001.Edge2,Bearing.Part__Feature001.Edge2]
  Reference2 = -> Assembly [Hub_Cage.Fillet.Edge137,Hub_Cage.Fillet.Edge137]
FEATURE [App::FeaturePython] Joint003  label="Fixed002"  # Assembly joint (typed FeaturePython)
  Activated = true
  AngleMax = 0
  AngleMin = 0
  Detach1 = false
  Detach2 = false
  Distance = 0
  Distance2 = 0
  EnableAngleMax = false
  EnableAngleMin = false
  EnableLengthMax = false
  EnableLengthMin = false
  JointType = 0 (Fixed)
  LengthMax = 0
  LengthMin = 0
  Placement1 = pos=(0.5,0,0) rot=(-0.707107,0,-0.707107;3.14159rad)
  Placement2 = pos=(-39.6,0,0) rot=(-0.707107,0,-0.707107;3.14159rad)
  Reference1 = -> Assembly [Bearing_Cover001.Pocket005.Edge3,Bearing_Cover001.Pocket005.Edge3]
  Reference2 = -> Assembly [Hub_Cage.Fillet.Edge126,Hub_Cage.Fillet.Edge126]
FEATURE [App::FeaturePython] Joint004  label="Fixed003"  # Assembly joint (typed FeaturePython)
  Activated = true
  AngleMax = 0
  AngleMin = 0
  Detach1 = false
  Detach2 = false
  Distance = 0
  Distance2 = 0
  EnableAngleMax = false
  EnableAngleMin = false
  EnableLengthMax = false
  EnableLengthMin = false
  JointType = 0 (Fixed)
  LengthMax = 0
  LengthMin = 0
  Placement1 = pos=(0.5,0,0) rot=(-0.707107,0,-0.707107;3.14159rad)
  Placement2 = pos=(39.6,0,0) rot=(-0.707107,0,-0.707107;3.14159rad)
  Reference1 = -> Assembly [Bearing_Cover.Pocket005.Edge3,Bearing_Cover.Pocket005.Edge3]
  Reference2 = -> Assembly [Hub_Cage.Fillet.Edge161,Hub_Cage.Fillet.Edge161]
FEATURE [App::FeaturePython] Joint005  label="Fixed004"  # Assembly joint (typed FeaturePython)
  Activated = true
  AngleMax = 0
  AngleMin = 0
  Detach1 = false
  Detach2 = false
  Distance = 0
  Distance2 = 0
  EnableAngleMax = false
  EnableAngleMin = false
  EnableLengthMax = false
  EnableLengthMin = false
  JointType = 0 (Fixed)
  LengthMax = 0
  LengthMin = 0
  Placement2 = pos=(10.9,0,0) rot=(-0.707107,0,-0.707107;3.14159rad)
  Reference1 = -> Assembly [M10_Washer.Edge5,M10_Washer.Edge5]
  Reference2 = -> Assembly [Bearing_Cover.Pocket005.Edge2,Bearing_Cover.Pocket005.Edge2]
FEATURE [App::FeaturePython] Joint006  label="Fixed005"  # Assembly joint (typed FeaturePython)
  Activated = true
  AngleMax = 0
  AngleMin = 0
  Detach1 = false
  Detach2 = false
  Distance = 0
  Distance2 = 0
  EnableAngleMax = false
  EnableAngleMin = false
  EnableLengthMax = false
  EnableLengthMin = false
  JointType = 0 (Fixed)
  LengthMax = 0
  LengthMin = 0
  Placement1 = pos=(0,0,2.6e-15) rot=(0.57735,-0.57735,0.57735;4.18879rad)
  Placement2 = pos=(4e-16,0,2) rot=(0,0,1;0rad)
  Reference1 = -> Assembly [Bolt_Cover.Fillet001.Edge13,Bolt_Cover.Fillet001.Edge13]
  Reference2 = -> Assembly [M10_Washer.Edge1,M10_Washer.Edge1]
FEATURE [App::FeaturePython] Joint007  label="Fixed006"  # Assembly joint (typed FeaturePython)
  Activated = true
  AngleMax = 0
  AngleMin = 0
  Detach1 = false
  Detach2 = false
  Distance = 0
  Distance2 = 0
  EnableAngleMax = false
  EnableAngleMin = false
  EnableLengthMax = false
  EnableLengthMin = false
  JointType = 0 (Fixed)
  LengthMax = 0
  LengthMin = 0
  Placement1 = pos=(2e-16,0,2) rot=(0,0,1;0rad)
  Placement2 = pos=(10.9,0,0) rot=(-0.707107,0,-0.707107;3.14159rad)
  Reference1 = -> Assembly [M10_Washer001.Edge1,M10_Washer001.Edge1]
  Reference2 = -> Assembly [Bearing_Cover001.Pocket005.Edge2,Bearing_Cover001.Pocket005.Edge2]
FEATURE [App::FeaturePython] Joint008  label="Fixed007"  # Assembly joint (typed FeaturePython)
  Activated = true
  AngleMax = 0
  AngleMin = 0
  Detach1 = false
  Detach2 = false
  Distance = 0
  Distance2 = 0
  EnableAngleMax = false
  EnableAngleMin = false
  EnableLengthMax = false
  EnableLengthMin = false
  JointType = 0 (Fixed)
  LengthMax = 0
  LengthMin = 0
  Placement1 = pos=(0,0,2.6e-15) rot=(-0.57735,0.57735,-0.57735;2.0944rad)
  Reference1 = -> Assembly [Bolt_Cover001.Fillet001.Edge13,Bolt_Cover001.Fillet001.Edge13]
  Reference2 = -> Assembly [M10_Washer001.Edge5,M10_Washer001.Edge5]
FEATURE [App::FeaturePython] Joint009  label="Fixed008"  # Assembly joint (typed FeaturePython)
  Activated = true
  AngleMax = 0
  AngleMin = 0
  Detach1 = false
  Detach2 = false
  Distance = 0
  Distance2 = 0
  EnableAngleMax = false
  EnableAngleMin = false
  EnableLengthMax = false
  EnableLengthMin = false
  JointType = 0 (Fixed)
  LengthMax = 0
  LengthMin = 0
  Placement2 = pos=(-1.2,0,2.3e-15) rot=(0.57735,-0.57735,-0.57735;2.0944rad)
  Reference1 = -> Assembly [M10x35_Screw.Edge30,M10x35_Screw.Edge30]
  Reference2 = -> Assembly [Bolt_Cover.Fillet001.Edge9,Bolt_Cover.Fillet001.Edge9]
FEATURE [App::FeaturePython] Joint010  label="Fixed009"  # Assembly joint (typed FeaturePython)
  Activated = true
  AngleMax = 0
  AngleMin = 0
  Detach1 = false
  Detach2 = false
  Distance = 0
  Distance2 = 0
  EnableAngleMax = false
  EnableAngleMin = false
  EnableLengthMax = false
  EnableLengthMin = false
  JointType = 0 (Fixed)
  LengthMax = 0
  LengthMin = 0
  Placement2 = pos=(-1.2,0,2.3e-15) rot=(0.57735,-0.57735,-0.57735;2.0944rad)
  Reference1 = -> Assembly [M10x35_Screw001.Edge30,M10x35_Screw001.Edge30]
  Reference2 = -> Assembly [Bolt_Cover001.Fillet001.Edge9,Bolt_Cover001.Fillet001.Edge9]
FEATURE [Assembly::JointGroup] Joints
  Group = -> [GroundedJoint,Joint,Joint001,Joint002,Joint003,Joint004,Joint005,Joint006,Joint007,Joint008,Joint009,Joint010]
FEATURE [App::FeaturePython] Move  # WARN: FeaturePython — macro-defined, semantics opaque (R4)
  MoveType = 1
  MovementTransform = pos=(31.0001,0,0) rot=(0,0,1;0rad)
  References = -> Assembly [Axle.,Hub_Cage.,Bearing.,Bearing001.,Bearing_Cover.,Bearing_Cover001.,M10_Washer.,M10_Washer001.,M10x35_Screw.,M10x35_Screw001.,Bolt_Cover.,Bolt_Cover001.]
FEATURE [App::FeaturePython] Move001  # WARN: FeaturePython — macro-defined, semantics opaque (R4)
  MoveType = 0
  MovementTransform = pos=(-63.0001,0,-1e-05) rot=(-1.00436,0,0;0rad)
  References = -> Assembly [M10x35_Screw001.]
FEATURE [App::FeaturePython] Move002  # WARN: FeaturePython — macro-defined, semantics opaque (R4)
  MoveType = 0
  MovementTransform = pos=(65.0001,-1e-05,0) rot=(-1.00436,0,0;0rad)
  References = -> Assembly [M10x35_Screw.]
FEATURE [App::FeaturePython] Exploded_View  # WARN: FeaturePython — macro-defined, semantics opaque (R4)
  Moves = -> [Move,Move001,Move002]
FEATURE [Assembly::ViewGroup] Exploded_Views
  Group = -> [Exploded_View]
FEATURE [Assembly::AssemblyObject] Assembly  label="Complete Hub"
  Group = -> [Joints,Axle,GroundedJoint,Hub_Cage,Bearing,Bearing001,Bearing_Cover,Bearing_Cover001,M10_Washer,M10_Washer001,M10x35_Screw,M10x35_Screw001,Bolt_Cover,Bolt_Cover001,Joint,Joint001,Joint002,Joint003,Joint004,Joint005,Joint006,Joint007,Joint008,Joint009,Joint010,Exploded_Views,Exploded_View,Move,Move001,Move002]
  Origin = -> Origin005
  Type = Assembly
